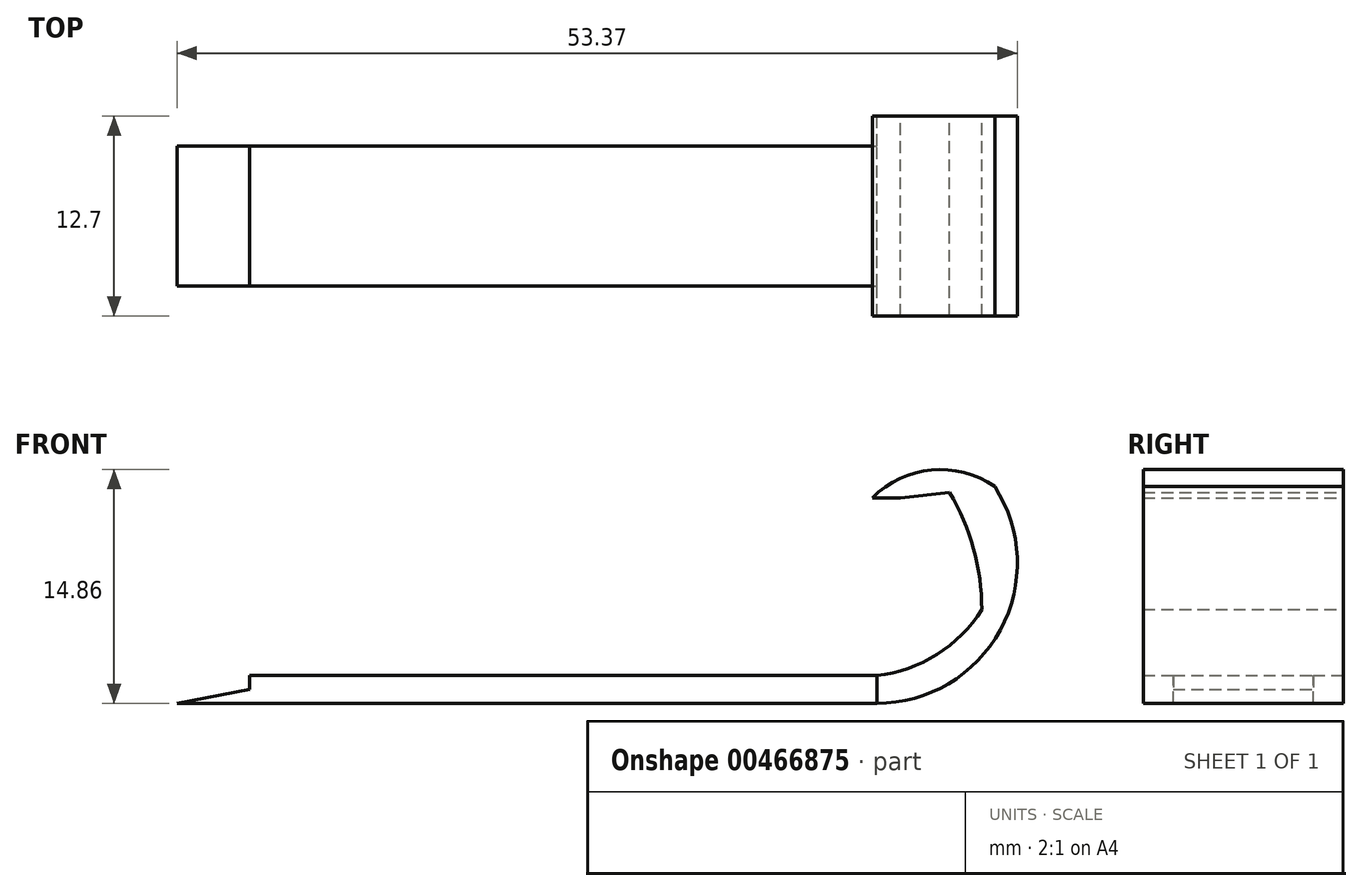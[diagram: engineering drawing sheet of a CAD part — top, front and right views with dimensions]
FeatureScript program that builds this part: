
annotation { "Feature Type Name" : "Feature", "Feature Type Description" : "" }
export const myFeature = defineFeature(function(context is Context, id is Id, definition is map)
    precondition{}
    {
        {
            var Q0;
            Q0=qCreatedBy(makeId("Front.planeOp"),FACE);
            var sketch = newSketch(context, id + "F0", { "sketchPlane" : qUnion([Q0])});
            skLineSegment(sketch, "E0.bottom", {"start": v(-49.5, 0) * mm, "end": v(-5.06, 0) * mm});
            skLineSegment(sketch, "E0.top", {"start": v(-44.9, 1.78) * mm, "end": v(-5.06, 1.78) * mm});
            skLineSegment(sketch, "E0.right", {"start": v(-5.06, 0) * mm, "end": v(-5.06, 1.78) * mm});
            skArc(sketch, "E1", {"start": v(-5.06, 1.78) * mm, "mid": v(-1.25, 3.11) * mm, "end": v(1.6, 5.97) * mm});
            skLineSegment(sketch, "E2", {"start": v(-5.06, 1.78) * mm, "end": v(1.6, 1.78) * mm, "construction": true});
            skLineSegment(sketch, "E3", {"start": v(1.6, 5.97) * mm, "end": v(1.6, 1.78) * mm, "construction": true});
            skLineSegment(sketch, "E4", {"start": v(-49.5, 0) * mm, "end": v(-44.9, 0.89) * mm});
            skLineSegment(sketch, "E5", {"start": v(-44.9, 1.78) * mm, "end": v(-44.9, 0.89) * mm});
            skPoint(sketch, "E6.visualSharp", {"position": v(1.6, 5.97) * mm});
            skArc(sketch, "E7", {"start": v(1.6, 5.97) * mm, "mid": v(1.08, 9.82) * mm, "end": v(-0.45, 13.4) * mm});
            skLineSegment(sketch, "E8", {"start": v(-5.35, 13.06) * mm, "end": v(-3.55, 13.06) * mm});
            skLineSegment(sketch, "E9", {"start": v(-3.55, 13.06) * mm, "end": v(-0.45, 13.4) * mm});
            skArc(sketch, "E10", {"start": v(-5.06, 0) * mm, "mid": v(2.78, 4.66) * mm, "end": v(2.43, 13.77) * mm});
            skArc(sketch, "E11", {"start": v(2.43, 13.77) * mm, "mid": v(-1.6, 14.83) * mm, "end": v(-5.35, 13.06) * mm});
            skPoint(sketch, "E12.orphan", {"position": v(3.36, 5.97) * mm});
            skSolve(sketch);
        }
        {
            var Q0;
            Q0=makeQuery(id+"F0.imprint","IMPRINT",FACE,{"disambiguationData":[TD([[makeQuery(id+"F0.imprint","IMPRINT",EDGE,{"derivedFrom":sQuery(id+"F0.wireOp",EDGE,"E0.right")}),-1.0]])]});
            extrude(context, id + "F1", {"entities" : qUnion([Q0]), "depth" : 12.7 * mm, "symmetric" : true});
        }
        {
            var Q0;
            Q0=makeQuery(id+"F0.imprint","IMPRINT",FACE,{"disambiguationData":[TD([[makeQuery(id+"F0.imprint","IMPRINT",EDGE,{"derivedFrom":sQuery(id+"F0.wireOp",EDGE,"E0.bottom")}),1.0]])]});
            extrude(context, id + "F2", {"entities" : qUnion([Q0]), "operationType" : NewBodyOperationType.ADD, "depth" : 8.9 * mm, "symmetric" : true});
        }
    });
